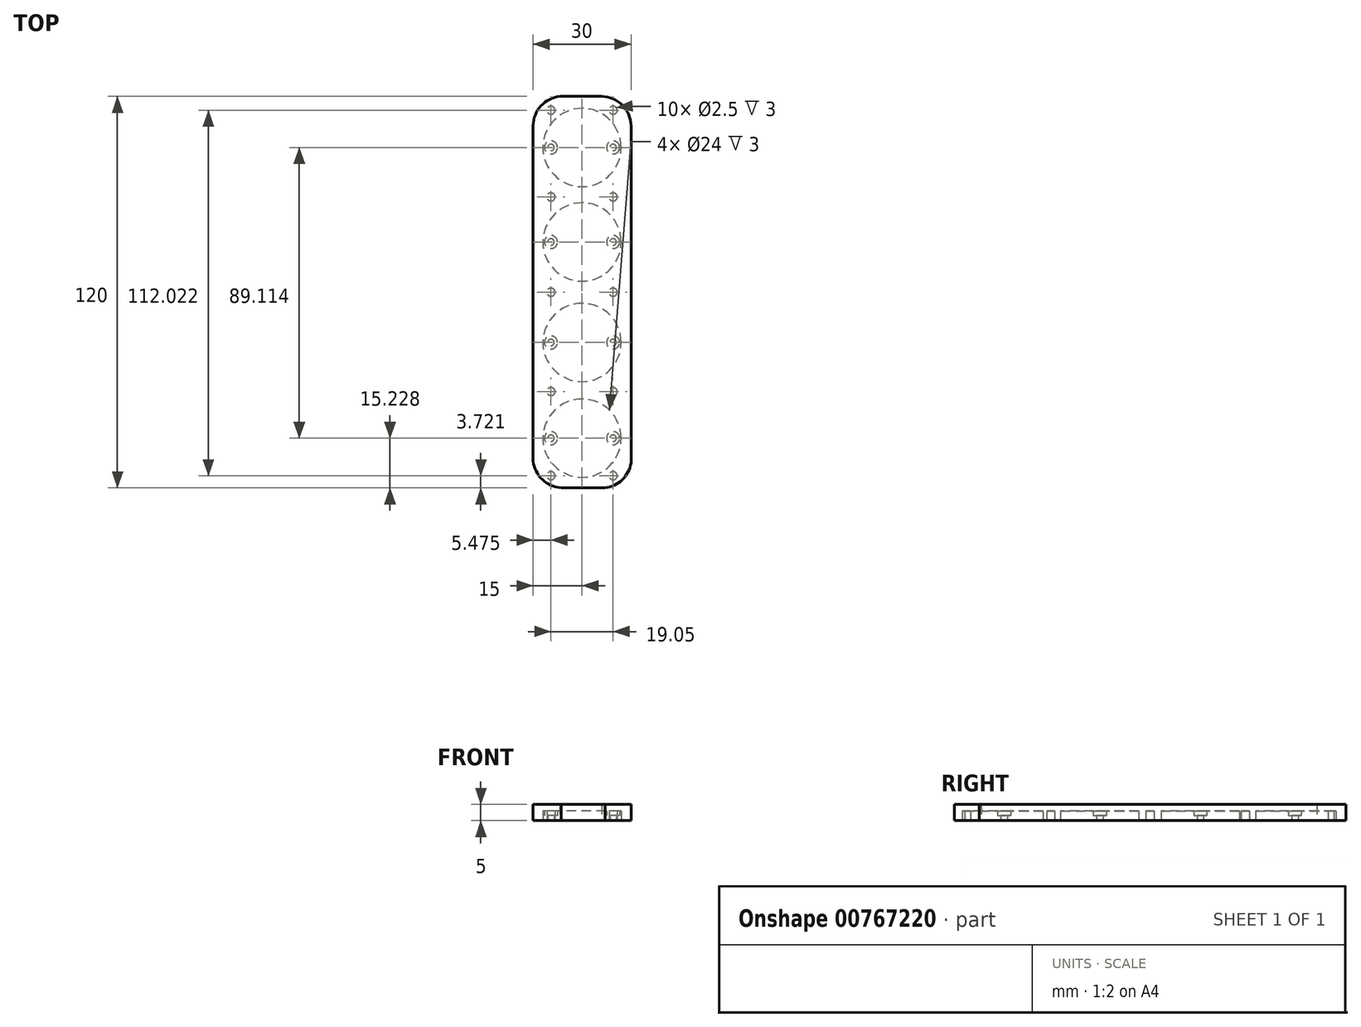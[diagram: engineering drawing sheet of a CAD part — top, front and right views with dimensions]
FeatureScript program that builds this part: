
annotation { "Feature Type Name" : "Feature", "Feature Type Description" : "" }
export const myFeature = defineFeature(function(context is Context, id is Id, definition is map)
    precondition{}
    {
        {
            var Q0;
            Q0=qCreatedBy(makeId("Top.planeOp"),FACE);
            var sketch = newSketch(context, id + "F0", { "sketchPlane" : qUnion([Q0])});
            skLineSegment(sketch, "E0.bottom", {"start": v(-15, 60.02) * mm, "end": v(15, 60.02) * mm});
            skLineSegment(sketch, "E0.top", {"start": v(-15, -59.98) * mm, "end": v(15, -59.98) * mm});
            skLineSegment(sketch, "E0.left", {"start": v(-15, 60.02) * mm, "end": v(-15, -59.98) * mm});
            skLineSegment(sketch, "E0.right", {"start": v(15, 60.02) * mm, "end": v(15, -59.98) * mm});
            skCircle(sketch, "E1", {"center": v(0, 44.36) * mm, "radius": 12 * mm});
            skCircle(sketch, "E2", {"center": v(0, 15.4) * mm, "radius": 12 * mm});
            skCircle(sketch, "E3", {"center": v(0, -15.42) * mm, "radius": 12 * mm});
            skCircle(sketch, "E4", {"center": v(0, -44.75) * mm, "radius": 12 * mm});
            skArc(sketch, "E5", {"start": v(-15, -49.5) * mm, "mid": v(-12.48, -57.1) * mm, "end": v(-5, -59.98) * mm});
            skArc(sketch, "E6", {"start": v(5, -59.98) * mm, "mid": v(12.6, -57.22) * mm, "end": v(15, -49.5) * mm});
            skArc(sketch, "E7", {"start": v(15, 50.8) * mm, "mid": v(12.4, 57.26) * mm, "end": v(6, 60.02) * mm});
            skArc(sketch, "E8", {"start": v(-5, 60.02) * mm, "mid": v(-12.07, 57.65) * mm, "end": v(-15, 50.8) * mm});
            skLineSegment(sketch, "E9", {"start": v(9.53, 68.25) * mm, "end": v(9.53, -73.05) * mm, "construction": true});
            skLineSegment(sketch, "E10", {"start": v(-9.53, 68.25) * mm, "end": v(-9.53, -73.05) * mm, "construction": true});
            skCircle(sketch, "E11", {"center": v(-9.53, 44.36) * mm, "radius": 1 * mm});
            skCircle(sketch, "E12", {"center": v(9.53, 44.36) * mm, "radius": 1 * mm});
            skCircle(sketch, "E13", {"center": v(9.53, 44.36) * mm, "radius": 2 * mm});
            skCircle(sketch, "E14", {"center": v(-9.53, 44.36) * mm, "radius": 2 * mm});
            skCircle(sketch, "E15", {"center": v(9.53, 15.4) * mm, "radius": 1 * mm});
            skCircle(sketch, "E16", {"center": v(9.53, 15.4) * mm, "radius": 2 * mm});
            skCircle(sketch, "E17", {"center": v(-9.53, 15.4) * mm, "radius": 1 * mm});
            skCircle(sketch, "E18", {"center": v(-9.53, 15.4) * mm, "radius": 2 * mm});
            skCircle(sketch, "E19", {"center": v(9.53, -15.42) * mm, "radius": 1 * mm});
            skCircle(sketch, "E20", {"center": v(9.53, -15.42) * mm, "radius": 2 * mm});
            skCircle(sketch, "E21", {"center": v(-9.53, -15.42) * mm, "radius": 1 * mm});
            skCircle(sketch, "E22", {"center": v(-9.53, -15.42) * mm, "radius": 2 * mm});
            skCircle(sketch, "E23", {"center": v(9.53, -44.75) * mm, "radius": 1 * mm});
            skCircle(sketch, "E24", {"center": v(9.53, -44.75) * mm, "radius": 2 * mm});
            skCircle(sketch, "E25", {"center": v(-9.53, -44.75) * mm, "radius": 1 * mm});
            skCircle(sketch, "E26", {"center": v(-9.53, -44.75) * mm, "radius": 2 * mm});
            skCircle(sketch, "E27", {"center": v(9.53, 55.76) * mm, "radius": 1.25 * mm});
            skCircle(sketch, "E28", {"center": v(-9.53, 55.76) * mm, "radius": 1.25 * mm});
            skCircle(sketch, "E29", {"center": v(9.53, 29.2) * mm, "radius": 1.25 * mm});
            skCircle(sketch, "E30", {"center": v(-9.53, 29.2) * mm, "radius": 1.25 * mm});
            skCircle(sketch, "E31", {"center": v(9.53, 0) * mm, "radius": 1.25 * mm});
            skCircle(sketch, "E32", {"center": v(-9.53, 0) * mm, "radius": 1.25 * mm});
            skCircle(sketch, "E33", {"center": v(9.53, -30.47) * mm, "radius": 1.25 * mm});
            skCircle(sketch, "E34", {"center": v(-9.53, -30.47) * mm, "radius": 1.25 * mm});
            skCircle(sketch, "E35", {"center": v(9.53, -56.26) * mm, "radius": 1.25 * mm});
            skCircle(sketch, "E36", {"center": v(-9.53, -56.26) * mm, "radius": 1.25 * mm});
            skSolve(sketch);
        }
        {
            var Q0;
            Q0=makeQuery(id+"F0.imprint","IMPRINT",FACE,{"disambiguationData":[TD([[makeQuery(id+"F0.imprint","IMPRINT",EDGE,{"derivedFrom":sQuery(id+"F0.wireOp",EDGE,"E1")}),-1.0]])]});
            extrude(context, id + "F1", {"entities" : qUnion([Q0]), "depth" : 5 * mm, "offsetDistance" : 25 * mm});
        }
        {
            var Q0;
            Q0=makeQuery(id+"F0.imprint","IMPRINT",FACE,{"disambiguationData":[TD([[makeQuery(id+"F0.imprint","IMPRINT",EDGE,{"derivedFrom":sQuery(id+"F0.wireOp",EDGE,"E1")}),1.0]])]});
            var Q1;
            Q1=makeQuery(id+"F0.imprint","IMPRINT",FACE,{"disambiguationData":[TD([[makeQuery(id+"F0.imprint","IMPRINT",EDGE,{"derivedFrom":sQuery(id+"F0.wireOp",EDGE,"E2")}),1.0]])]});
            var Q2;
            Q2=makeQuery(id+"F0.imprint","IMPRINT",FACE,{"disambiguationData":[TD([[makeQuery(id+"F0.imprint","IMPRINT",EDGE,{"derivedFrom":sQuery(id+"F0.wireOp",EDGE,"E3")}),1.0]])]});
            var Q3;
            Q3=makeQuery(id+"F0.imprint","IMPRINT",FACE,{"disambiguationData":[TD([[makeQuery(id+"F0.imprint","IMPRINT",EDGE,{"derivedFrom":sQuery(id+"F0.wireOp",EDGE,"E4")}),1.0]])]});
            var Q4;
            Q4=makeQuery(id+"F0.imprint","IMPRINT",FACE,{"disambiguationData":[TD([[makeQuery(id+"F0.imprint","IMPRINT",EDGE,{"derivedFrom":sQuery(id+"F0.wireOp",EDGE,"E12")}),1.0]])]});
            var Q5;
            Q5=makeQuery(id+"F0.imprint","IMPRINT",FACE,{"disambiguationData":[TD([[makeQuery(id+"F0.imprint","IMPRINT",EDGE,{"derivedFrom":sQuery(id+"F0.wireOp",EDGE,"E12")}),-1.0]])]});
            var Q6;
            Q6=makeQuery(id+"F0.imprint","IMPRINT",FACE,{"disambiguationData":[TD([[makeQuery(id+"F0.imprint","IMPRINT",EDGE,{"derivedFrom":sQuery(id+"F0.wireOp",EDGE,"E11")}),1.0]])]});
            var Q7;
            Q7=makeQuery(id+"F0.imprint","IMPRINT",FACE,{"disambiguationData":[TD([[makeQuery(id+"F0.imprint","IMPRINT",EDGE,{"derivedFrom":sQuery(id+"F0.wireOp",EDGE,"E11")}),-1.0]])]});
            var Q8;
            Q8=makeQuery(id+"F0.imprint","IMPRINT",FACE,{"disambiguationData":[TD([[makeQuery(id+"F0.imprint","IMPRINT",EDGE,{"derivedFrom":sQuery(id+"F0.wireOp",EDGE,"E15")}),1.0]])]});
            var Q9;
            Q9=makeQuery(id+"F0.imprint","IMPRINT",FACE,{"disambiguationData":[TD([[makeQuery(id+"F0.imprint","IMPRINT",EDGE,{"derivedFrom":sQuery(id+"F0.wireOp",EDGE,"E15")}),-1.0]])]});
            var Q10;
            Q10=makeQuery(id+"F0.imprint","IMPRINT",FACE,{"disambiguationData":[TD([[makeQuery(id+"F0.imprint","IMPRINT",EDGE,{"derivedFrom":sQuery(id+"F0.wireOp",EDGE,"E17")}),1.0]])]});
            var Q11;
            Q11=makeQuery(id+"F0.imprint","IMPRINT",FACE,{"disambiguationData":[TD([[makeQuery(id+"F0.imprint","IMPRINT",EDGE,{"derivedFrom":sQuery(id+"F0.wireOp",EDGE,"E17")}),-1.0]])]});
            var Q12;
            Q12=makeQuery(id+"F0.imprint","IMPRINT",FACE,{"disambiguationData":[TD([[makeQuery(id+"F0.imprint","IMPRINT",EDGE,{"derivedFrom":sQuery(id+"F0.wireOp",EDGE,"E19")}),1.0]])]});
            var Q13;
            Q13=makeQuery(id+"F0.imprint","IMPRINT",FACE,{"disambiguationData":[TD([[makeQuery(id+"F0.imprint","IMPRINT",EDGE,{"derivedFrom":sQuery(id+"F0.wireOp",EDGE,"E19")}),-1.0]])]});
            var Q14;
            Q14=makeQuery(id+"F0.imprint","IMPRINT",FACE,{"disambiguationData":[TD([[makeQuery(id+"F0.imprint","IMPRINT",EDGE,{"derivedFrom":sQuery(id+"F0.wireOp",EDGE,"E21")}),1.0]])]});
            var Q15;
            Q15=makeQuery(id+"F0.imprint","IMPRINT",FACE,{"disambiguationData":[TD([[makeQuery(id+"F0.imprint","IMPRINT",EDGE,{"derivedFrom":sQuery(id+"F0.wireOp",EDGE,"E21")}),-1.0]])]});
            var Q16;
            Q16=makeQuery(id+"F0.imprint","IMPRINT",FACE,{"disambiguationData":[TD([[makeQuery(id+"F0.imprint","IMPRINT",EDGE,{"derivedFrom":sQuery(id+"F0.wireOp",EDGE,"E23")}),1.0]])]});
            var Q17;
            Q17=makeQuery(id+"F0.imprint","IMPRINT",FACE,{"disambiguationData":[TD([[makeQuery(id+"F0.imprint","IMPRINT",EDGE,{"derivedFrom":sQuery(id+"F0.wireOp",EDGE,"E23")}),-1.0]])]});
            var Q18;
            Q18=makeQuery(id+"F0.imprint","IMPRINT",FACE,{"disambiguationData":[TD([[makeQuery(id+"F0.imprint","IMPRINT",EDGE,{"derivedFrom":sQuery(id+"F0.wireOp",EDGE,"E25")}),-1.0]])]});
            var Q19;
            Q19=makeQuery(id+"F0.imprint","IMPRINT",FACE,{"disambiguationData":[TD([[makeQuery(id+"F0.imprint","IMPRINT",EDGE,{"derivedFrom":sQuery(id+"F0.wireOp",EDGE,"E25")}),1.0]])]});
            var Q20;
            Q20=makeQuery(id+"F0.imprint","IMPRINT",FACE,{"disambiguationData":[TD([[makeQuery(id+"F0.imprint","IMPRINT",EDGE,{"derivedFrom":sQuery(id+"F0.wireOp",EDGE,"E35")}),1.0]])]});
            var Q21;
            Q21=makeQuery(id+"F0.imprint","IMPRINT",FACE,{"disambiguationData":[TD([[makeQuery(id+"F0.imprint","IMPRINT",EDGE,{"derivedFrom":sQuery(id+"F0.wireOp",EDGE,"E36")}),1.0]])]});
            var Q22;
            Q22=makeQuery(id+"F0.imprint","IMPRINT",FACE,{"disambiguationData":[TD([[makeQuery(id+"F0.imprint","IMPRINT",EDGE,{"derivedFrom":sQuery(id+"F0.wireOp",EDGE,"E34")}),1.0]])]});
            var Q23;
            Q23=makeQuery(id+"F0.imprint","IMPRINT",FACE,{"disambiguationData":[TD([[makeQuery(id+"F0.imprint","IMPRINT",EDGE,{"derivedFrom":sQuery(id+"F0.wireOp",EDGE,"E33")}),1.0]])]});
            var Q24;
            Q24=makeQuery(id+"F0.imprint","IMPRINT",FACE,{"disambiguationData":[TD([[makeQuery(id+"F0.imprint","IMPRINT",EDGE,{"derivedFrom":sQuery(id+"F0.wireOp",EDGE,"E31")}),1.0]])]});
            var Q25;
            Q25=makeQuery(id+"F0.imprint","IMPRINT",FACE,{"disambiguationData":[TD([[makeQuery(id+"F0.imprint","IMPRINT",EDGE,{"derivedFrom":sQuery(id+"F0.wireOp",EDGE,"E32")}),1.0]])]});
            var Q26;
            Q26=makeQuery(id+"F0.imprint","IMPRINT",FACE,{"disambiguationData":[TD([[makeQuery(id+"F0.imprint","IMPRINT",EDGE,{"derivedFrom":sQuery(id+"F0.wireOp",EDGE,"E30")}),1.0]])]});
            var Q27;
            Q27=makeQuery(id+"F0.imprint","IMPRINT",FACE,{"disambiguationData":[TD([[makeQuery(id+"F0.imprint","IMPRINT",EDGE,{"derivedFrom":sQuery(id+"F0.wireOp",EDGE,"E29")}),1.0]])]});
            var Q28;
            Q28=makeQuery(id+"F0.imprint","IMPRINT",FACE,{"disambiguationData":[TD([[makeQuery(id+"F0.imprint","IMPRINT",EDGE,{"derivedFrom":sQuery(id+"F0.wireOp",EDGE,"E28")}),1.0]])]});
            var Q29;
            Q29=makeQuery(id+"F0.imprint","IMPRINT",FACE,{"disambiguationData":[TD([[makeQuery(id+"F0.imprint","IMPRINT",EDGE,{"derivedFrom":sQuery(id+"F0.wireOp",EDGE,"E27")}),1.0]])]});
            extrude(context, id + "F2", {"entities" : qUnion([Q0, Q1, Q2, Q3, Q4, Q5, Q6, Q7, Q8, Q9, Q10, Q11, Q12, Q13, Q14, Q15, Q16, Q17, Q18, Q19, Q20, Q21, Q22, Q23, Q24, Q25, Q26, Q27, Q28, Q29]), "operationType" : NewBodyOperationType.ADD, "depth" : 5 * mm, "offsetDistance" : 25 * mm, "hasSecondDirection" : true, "secondDirectionOppositeDirection" : false, "secondDirectionDepth" : 3 * mm});
        }
        {
            var Q0;
            Q0=makeQuery(id+"F0.imprint","IMPRINT",FACE,{"disambiguationData":[TD([[makeQuery(id+"F0.imprint","IMPRINT",EDGE,{"derivedFrom":sQuery(id+"F0.wireOp",EDGE,"E12")}),1.0]])]});
            var Q1;
            Q1=makeQuery(id+"F0.imprint","IMPRINT",FACE,{"disambiguationData":[TD([[makeQuery(id+"F0.imprint","IMPRINT",EDGE,{"derivedFrom":sQuery(id+"F0.wireOp",EDGE,"E11")}),1.0]])]});
            var Q2;
            Q2=makeQuery(id+"F0.imprint","IMPRINT",FACE,{"disambiguationData":[TD([[makeQuery(id+"F0.imprint","IMPRINT",EDGE,{"derivedFrom":sQuery(id+"F0.wireOp",EDGE,"E15")}),1.0]])]});
            var Q3;
            Q3=makeQuery(id+"F0.imprint","IMPRINT",FACE,{"disambiguationData":[TD([[makeQuery(id+"F0.imprint","IMPRINT",EDGE,{"derivedFrom":sQuery(id+"F0.wireOp",EDGE,"E17")}),1.0]])]});
            var Q4;
            Q4=makeQuery(id+"F0.imprint","IMPRINT",FACE,{"disambiguationData":[TD([[makeQuery(id+"F0.imprint","IMPRINT",EDGE,{"derivedFrom":sQuery(id+"F0.wireOp",EDGE,"E19")}),1.0]])]});
            var Q5;
            Q5=makeQuery(id+"F0.imprint","IMPRINT",FACE,{"disambiguationData":[TD([[makeQuery(id+"F0.imprint","IMPRINT",EDGE,{"derivedFrom":sQuery(id+"F0.wireOp",EDGE,"E21")}),1.0]])]});
            var Q6;
            Q6=makeQuery(id+"F0.imprint","IMPRINT",FACE,{"disambiguationData":[TD([[makeQuery(id+"F0.imprint","IMPRINT",EDGE,{"derivedFrom":sQuery(id+"F0.wireOp",EDGE,"E23")}),1.0]])]});
            var Q7;
            Q7=makeQuery(id+"F0.imprint","IMPRINT",FACE,{"disambiguationData":[TD([[makeQuery(id+"F0.imprint","IMPRINT",EDGE,{"derivedFrom":sQuery(id+"F0.wireOp",EDGE,"E25")}),1.0]])]});
            extrude(context, id + "F3", {"entities" : qUnion([Q0, Q1, Q2, Q3, Q4, Q5, Q6, Q7]), "operationType" : NewBodyOperationType.ADD, "depth" : 5 * mm, "offsetDistance" : 25 * mm, "hasSecondDirection" : true, "secondDirectionOppositeDirection" : true, "secondDirectionDepth" : 0 * mm});
        }
        {
            var Q0;
            Q0=makeQuery(id+"F0.imprint","IMPRINT",FACE,{"disambiguationData":[TD([[makeQuery(id+"F0.imprint","IMPRINT",EDGE,{"derivedFrom":sQuery(id+"F0.wireOp",EDGE,"E12")}),-1.0]])]});
            var Q1;
            Q1=makeQuery(id+"F0.imprint","IMPRINT",FACE,{"disambiguationData":[TD([[makeQuery(id+"F0.imprint","IMPRINT",EDGE,{"derivedFrom":sQuery(id+"F0.wireOp",EDGE,"E11")}),-1.0]])]});
            var Q2;
            Q2=makeQuery(id+"F0.imprint","IMPRINT",FACE,{"disambiguationData":[TD([[makeQuery(id+"F0.imprint","IMPRINT",EDGE,{"derivedFrom":sQuery(id+"F0.wireOp",EDGE,"E15")}),-1.0]])]});
            var Q3;
            Q3=makeQuery(id+"F0.imprint","IMPRINT",FACE,{"disambiguationData":[TD([[makeQuery(id+"F0.imprint","IMPRINT",EDGE,{"derivedFrom":sQuery(id+"F0.wireOp",EDGE,"E17")}),-1.0]])]});
            var Q4;
            Q4=makeQuery(id+"F0.imprint","IMPRINT",FACE,{"disambiguationData":[TD([[makeQuery(id+"F0.imprint","IMPRINT",EDGE,{"derivedFrom":sQuery(id+"F0.wireOp",EDGE,"E19")}),-1.0]])]});
            var Q5;
            Q5=makeQuery(id+"F0.imprint","IMPRINT",FACE,{"disambiguationData":[TD([[makeQuery(id+"F0.imprint","IMPRINT",EDGE,{"derivedFrom":sQuery(id+"F0.wireOp",EDGE,"E21")}),-1.0]])]});
            var Q6;
            Q6=makeQuery(id+"F0.imprint","IMPRINT",FACE,{"disambiguationData":[TD([[makeQuery(id+"F0.imprint","IMPRINT",EDGE,{"derivedFrom":sQuery(id+"F0.wireOp",EDGE,"E23")}),-1.0]])]});
            var Q7;
            Q7=makeQuery(id+"F0.imprint","IMPRINT",FACE,{"disambiguationData":[TD([[makeQuery(id+"F0.imprint","IMPRINT",EDGE,{"derivedFrom":sQuery(id+"F0.wireOp",EDGE,"E25")}),-1.0]])]});
            extrude(context, id + "F4", {"entities" : qUnion([Q0, Q1, Q2, Q3, Q4, Q5, Q6, Q7]), "operationType" : NewBodyOperationType.ADD, "depth" : 5 * mm, "offsetDistance" : 25 * mm, "hasSecondDirection" : true, "secondDirectionOppositeDirection" : false, "secondDirectionDepth" : 1.6 * mm});
        }
        {
            var Q0;
            Q0=makeQuery(id+"F0.imprint","IMPRINT",FACE,{"disambiguationData":[TD([[makeQuery(id+"F0.imprint","IMPRINT",EDGE,{"derivedFrom":sQuery(id+"F0.wireOp",EDGE,"E35")}),1.0]])]});
            var Q1;
            Q1=makeQuery(id+"F0.imprint","IMPRINT",FACE,{"disambiguationData":[TD([[makeQuery(id+"F0.imprint","IMPRINT",EDGE,{"derivedFrom":sQuery(id+"F0.wireOp",EDGE,"E36")}),1.0]])]});
            var Q2;
            Q2=makeQuery(id+"F0.imprint","IMPRINT",FACE,{"disambiguationData":[TD([[makeQuery(id+"F0.imprint","IMPRINT",EDGE,{"derivedFrom":sQuery(id+"F0.wireOp",EDGE,"E34")}),1.0]])]});
            var Q3;
            Q3=makeQuery(id+"F0.imprint","IMPRINT",FACE,{"disambiguationData":[TD([[makeQuery(id+"F0.imprint","IMPRINT",EDGE,{"derivedFrom":sQuery(id+"F0.wireOp",EDGE,"E33")}),1.0]])]});
            var Q4;
            Q4=makeQuery(id+"F0.imprint","IMPRINT",FACE,{"disambiguationData":[TD([[makeQuery(id+"F0.imprint","IMPRINT",EDGE,{"derivedFrom":sQuery(id+"F0.wireOp",EDGE,"E31")}),1.0]])]});
            var Q5;
            Q5=makeQuery(id+"F0.imprint","IMPRINT",FACE,{"disambiguationData":[TD([[makeQuery(id+"F0.imprint","IMPRINT",EDGE,{"derivedFrom":sQuery(id+"F0.wireOp",EDGE,"E32")}),1.0]])]});
            var Q6;
            Q6=makeQuery(id+"F0.imprint","IMPRINT",FACE,{"disambiguationData":[TD([[makeQuery(id+"F0.imprint","IMPRINT",EDGE,{"derivedFrom":sQuery(id+"F0.wireOp",EDGE,"E29")}),1.0]])]});
            var Q7;
            Q7=makeQuery(id+"F0.imprint","IMPRINT",FACE,{"disambiguationData":[TD([[makeQuery(id+"F0.imprint","IMPRINT",EDGE,{"derivedFrom":sQuery(id+"F0.wireOp",EDGE,"E30")}),1.0]])]});
            var Q8;
            Q8=makeQuery(id+"F0.imprint","IMPRINT",FACE,{"disambiguationData":[TD([[makeQuery(id+"F0.imprint","IMPRINT",EDGE,{"derivedFrom":sQuery(id+"F0.wireOp",EDGE,"E27")}),1.0]])]});
            var Q9;
            Q9=makeQuery(id+"F0.imprint","IMPRINT",FACE,{"disambiguationData":[TD([[makeQuery(id+"F0.imprint","IMPRINT",EDGE,{"derivedFrom":sQuery(id+"F0.wireOp",EDGE,"E28")}),1.0]])]});
            extrude(context, id + "F5", {"entities" : qUnion([Q0, Q1, Q2, Q3, Q4, Q5, Q6, Q7, Q8, Q9]), "operationType" : NewBodyOperationType.REMOVE, "depth" : 1.3 * mm, "offsetDistance" : 25 * mm, "hasSecondDirection" : true, "secondDirectionOppositeDirection" : true, "secondDirectionDepth" : 0.1 * mm});
        }
    });
